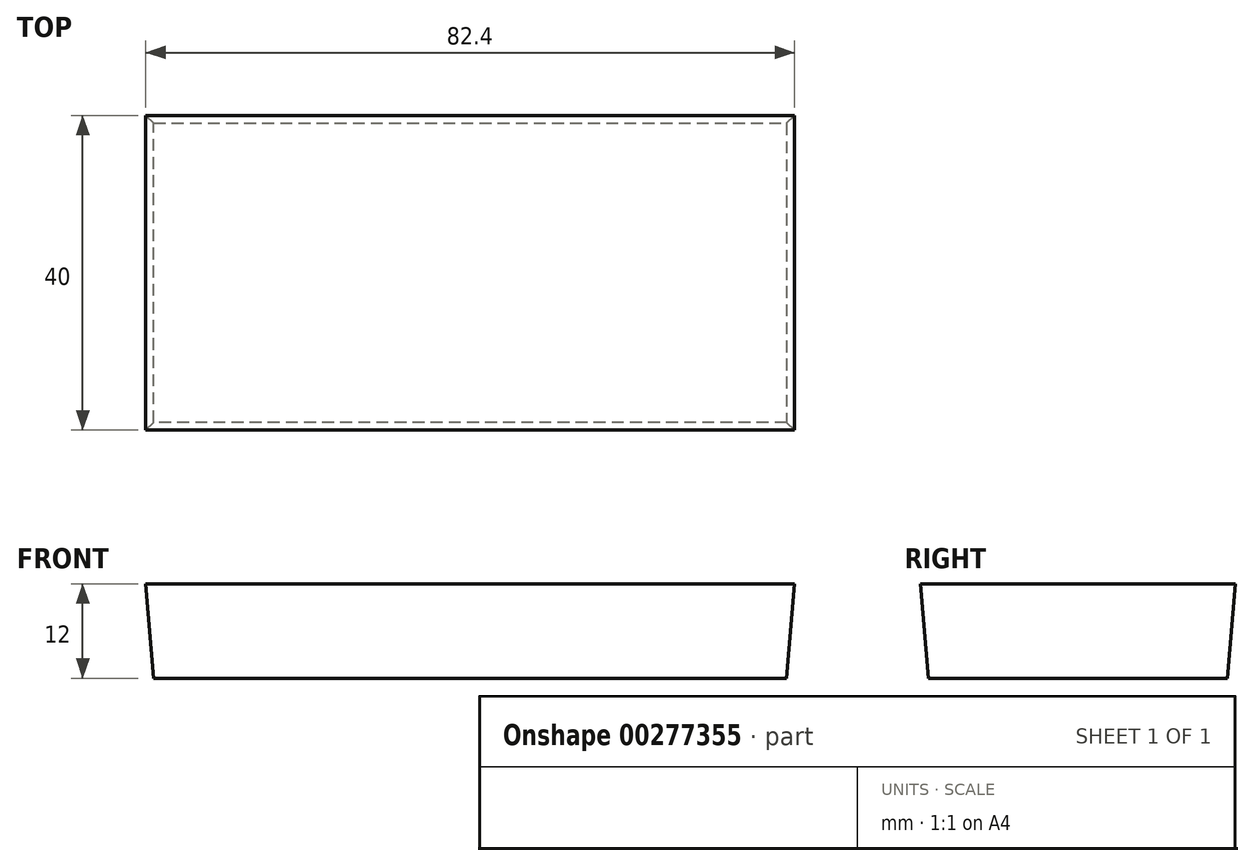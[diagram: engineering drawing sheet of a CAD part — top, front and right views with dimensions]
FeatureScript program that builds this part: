
annotation { "Feature Type Name" : "Feature", "Feature Type Description" : "" }
export const myFeature = defineFeature(function(context is Context, id is Id, definition is map)
    precondition{}
    {
        {
            var Q0;
            Q0=qCreatedBy(makeId("Top.planeOp"),FACE);
            var sketch = newSketch(context, id + "F0", { "sketchPlane" : qUnion([Q0])});
            skLineSegment(sketch, "E0.bottom", {"start": v(41.2, -20) * mm, "end": v(-41.2, -20) * mm});
            skLineSegment(sketch, "E0.top", {"start": v(41.2, 20) * mm, "end": v(-41.2, 20) * mm});
            skLineSegment(sketch, "E0.left", {"start": v(41.2, -20) * mm, "end": v(41.2, 20) * mm});
            skLineSegment(sketch, "E0.right", {"start": v(-41.2, -20) * mm, "end": v(-41.2, 20) * mm});
            skPoint(sketch, "E0.middle", {"position": v(0, 0) * mm});
            skSolve(sketch);
        }
        {
            var Q0;
            Q0 = qSketchRegion(id + "F0", true);
            extrude(context, id + "F1", {"entities" : qUnion([Q0]), "depth" : 12 * mm});
        }
        {
            var Q0;
            Q0=makeQuery(id+"F1.opExtrude","CAP_FACE",FACE,{"disambiguationData":[OSD([sQuery(id+"F0.wireOp",EDGE,"E0.bottom"),sQuery(id+"F0.wireOp",EDGE,"E0.top"),sQuery(id+"F0.wireOp",EDGE,"E0.left"),sQuery(id+"F0.wireOp",EDGE,"E0.right")])],"isStart":true});
            chamfer(context, id + "F2", {"entities" : qUnion([Q0]), "chamferType" : ChamferType.TWO_OFFSETS, "width1" : 1 * mm, "oppositeDirection" : false, "width2" : 12 * mm, "tangentPropagation" : true});
        }
    });
